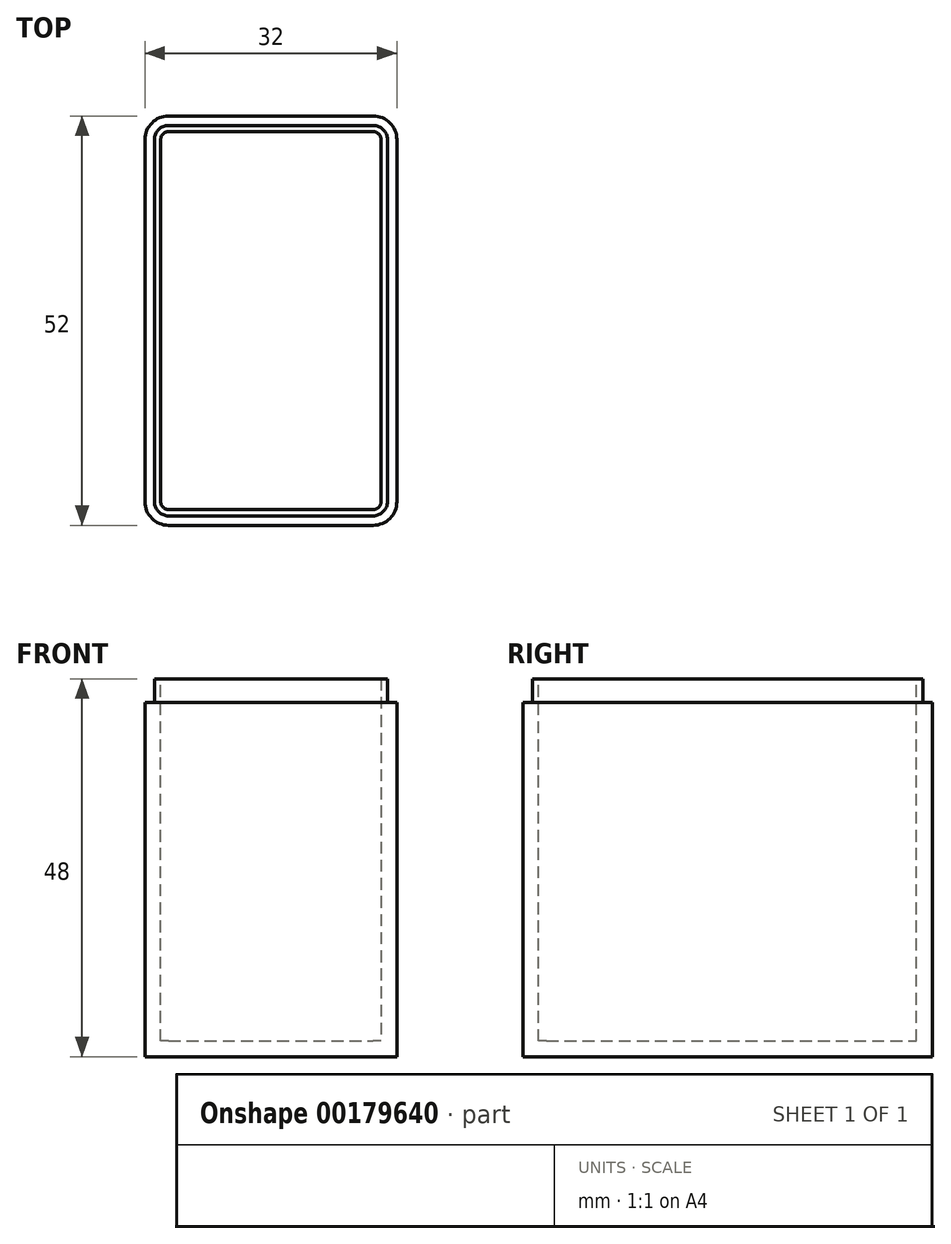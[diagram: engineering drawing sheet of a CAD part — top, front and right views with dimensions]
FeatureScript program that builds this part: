
annotation { "Feature Type Name" : "Feature", "Feature Type Description" : "" }
export const myFeature = defineFeature(function(context is Context, id is Id, definition is map)
    precondition{}
    {
        {
            var Q0;
            Q0=qCreatedBy(makeId("Top.planeOp"),FACE);
            var sketch = newSketch(context, id + "F0", { "sketchPlane" : qUnion([Q0])});
            skLineSegment(sketch, "E0.bottom", {"start": v(3, 0) * mm, "end": v(29, 0) * mm});
            skLineSegment(sketch, "E0.top", {"start": v(3, 52) * mm, "end": v(29, 52) * mm});
            skLineSegment(sketch, "E0.left", {"start": v(0, 3) * mm, "end": v(0, 49) * mm});
            skLineSegment(sketch, "E0.right", {"start": v(32, 3) * mm, "end": v(32, 49) * mm});
            skPoint(sketch, "E1.visualSharp", {"position": v(0, 52) * mm});
            skArc(sketch, "E1.filletArc", {"start": v(3, 52) * mm, "mid": v(0.88, 51.12) * mm, "end": v(0, 49) * mm});
            skPoint(sketch, "E2.visualSharp", {"position": v(32, 52) * mm});
            skArc(sketch, "E2.filletArc", {"start": v(32, 49) * mm, "mid": v(31.12, 51.12) * mm, "end": v(29, 52) * mm});
            skPoint(sketch, "E3.visualSharp", {"position": v(32, 0) * mm});
            skArc(sketch, "E3.filletArc", {"start": v(29, 0) * mm, "mid": v(31.12, 0.88) * mm, "end": v(32, 3) * mm});
            skPoint(sketch, "E4.visualSharp", {"position": v(0, 0) * mm});
            skArc(sketch, "E4.filletArc", {"start": v(0, 3) * mm, "mid": v(0.88, 0.88) * mm, "end": v(3, 0) * mm});
            skSolve(sketch);
        }
        {
            var Q0;
            Q0=makeQuery(id+"F0.imprint","IMPRINT",FACE,{"disambiguationData":[TD([[makeQuery(id+"F0.imprint","IMPRINT",EDGE,{"derivedFrom":sQuery(id+"F0.wireOp",EDGE,"E0.bottom")}),1.0]])]});
            extrude(context, id + "F1", {"entities" : qUnion([Q0]), "depth" : 45 * mm});
        }
        {
            var Q0;
            Q0=makeQuery(id+"F1.opExtrude","CAP_FACE",FACE,{"disambiguationData":[OSD([sQuery(id+"F0.wireOp",EDGE,"E0.bottom"),sQuery(id+"F0.wireOp",EDGE,"E0.top"),sQuery(id+"F0.wireOp",EDGE,"E0.left"),sQuery(id+"F0.wireOp",EDGE,"E0.right"),sQuery(id+"F0.wireOp",EDGE,"E1.filletArc"),sQuery(id+"F0.wireOp",EDGE,"E2.filletArc"),sQuery(id+"F0.wireOp",EDGE,"E3.filletArc"),sQuery(id+"F0.wireOp",EDGE,"E4.filletArc")])],"isStart":false});
            shell(context, id + "F2", {"entities" : qUnion([Q0]), "thickness" : 2 * mm});
        }
        {
            var Q0;
            Q0=makeQuery(id+"F1.opExtrude","CAP_FACE",FACE,{"disambiguationData":[OSD([sQuery(id+"F0.wireOp",EDGE,"E0.bottom"),sQuery(id+"F0.wireOp",EDGE,"E0.top"),sQuery(id+"F0.wireOp",EDGE,"E0.left"),sQuery(id+"F0.wireOp",EDGE,"E0.right"),sQuery(id+"F0.wireOp",EDGE,"E1.filletArc"),sQuery(id+"F0.wireOp",EDGE,"E2.filletArc"),sQuery(id+"F0.wireOp",EDGE,"E3.filletArc"),sQuery(id+"F0.wireOp",EDGE,"E4.filletArc")])],"isStart":false});
            var sketch = newSketch(context, id + "F3", { "sketchPlane" : qUnion([Q0])});
            skLineSegment(sketch, "E5.0", {"start": v(3, 2) * mm, "end": v(29, 2) * mm});
            skArc(sketch, "E6.0", {"start": v(2, 3) * mm, "mid": v(2.3, 2.3) * mm, "end": v(3, 2) * mm});
            skLineSegment(sketch, "E7.0", {"start": v(2, 3) * mm, "end": v(2, 49) * mm});
            skArc(sketch, "E8.0", {"start": v(3, 50) * mm, "mid": v(2.3, 49.7) * mm, "end": v(2, 49) * mm});
            skLineSegment(sketch, "E9.0", {"start": v(3, 50) * mm, "end": v(29, 50) * mm});
            skArc(sketch, "E10.0", {"start": v(30, 49) * mm, "mid": v(29.7, 49.7) * mm, "end": v(29, 50) * mm});
            skLineSegment(sketch, "E11.0", {"start": v(30, 3) * mm, "end": v(30, 49) * mm});
            skArc(sketch, "E12.0", {"start": v(29, 2) * mm, "mid": v(29.7, 2.3) * mm, "end": v(30, 3) * mm});
            skArc(sketch, "E13.0", {"start": v(29, 0) * mm, "mid": v(31.12, 0.88) * mm, "end": v(32, 3) * mm});
            skArc(sketch, "E14.0", {"start": v(0, 3) * mm, "mid": v(0.88, 0.88) * mm, "end": v(3, 0) * mm});
            skArc(sketch, "E15.0", {"start": v(3, 52) * mm, "mid": v(0.88, 51.12) * mm, "end": v(0, 49) * mm});
            skArc(sketch, "E16.0", {"start": v(32, 49) * mm, "mid": v(31.12, 51.12) * mm, "end": v(29, 52) * mm});
            skLineSegment(sketch, "E17.0", {"start": v(3, 52) * mm, "end": v(29, 52) * mm});
            skLineSegment(sketch, "E18.0", {"start": v(32, 3) * mm, "end": v(32, 49) * mm});
            skLineSegment(sketch, "E19.0", {"start": v(0, 3) * mm, "end": v(0, 49) * mm});
            skLineSegment(sketch, "E20.0", {"start": v(3, 0) * mm, "end": v(29, 0) * mm});
            skLineSegment(sketch, "E21.0", {"start": v(3, 50.8) * mm, "end": v(29, 50.8) * mm});
            skArc(sketch, "E21.1", {"start": v(30.8, 49) * mm, "mid": v(30.27, 50.27) * mm, "end": v(29, 50.8) * mm});
            skArc(sketch, "E21.2", {"start": v(3, 50.8) * mm, "mid": v(1.73, 50.27) * mm, "end": v(1.2, 49) * mm});
            skLineSegment(sketch, "E21.3", {"start": v(30.8, 3) * mm, "end": v(30.8, 49) * mm});
            skLineSegment(sketch, "E21.4", {"start": v(1.2, 3) * mm, "end": v(1.2, 49) * mm});
            skArc(sketch, "E21.5", {"start": v(1.2, 3) * mm, "mid": v(1.73, 1.73) * mm, "end": v(3, 1.2) * mm});
            skLineSegment(sketch, "E21.6", {"start": v(3, 1.2) * mm, "end": v(29, 1.2) * mm});
            skArc(sketch, "E21.7", {"start": v(29, 1.2) * mm, "mid": v(30.27, 1.73) * mm, "end": v(30.8, 3) * mm});
            skSolve(sketch);
        }
        {
            var Q0;
            Q0=makeQuery(id+"F3.imprint","IMPRINT",FACE,{"disambiguationData":[TD([[makeQuery(id+"F3.imprint","IMPRINT",EDGE,{"derivedFrom":sQuery(id+"F3.wireOp",EDGE,"E5.0")}),-1.0]])]});
            var Q1;
            Q1=sQuery(id+"F3.wireOp",EDGE,"E9.0");
            var Q2;
            Q2=sQuery(id+"F3.wireOp",EDGE,"E21.0");
            var Q3;
            Q3=sQuery(id+"F3.wireOp",EDGE,"E21.2");
            var Q4;
            Q4=sQuery(id+"F3.wireOp",EDGE,"E8.0");
            var Q5;
            Q5=sQuery(id+"F3.wireOp",EDGE,"E21.4");
            var Q6;
            Q6=sQuery(id+"F3.wireOp",EDGE,"E7.0");
            var Q7;
            Q7=sQuery(id+"F3.wireOp",EDGE,"E10.0");
            var Q8;
            Q8=sQuery(id+"F3.wireOp",EDGE,"E21.1");
            var Q9;
            Q9=sQuery(id+"F3.wireOp",EDGE,"E21.3");
            var Q10;
            Q10=sQuery(id+"F3.wireOp",EDGE,"E11.0");
            var Q11;
            Q11=sQuery(id+"F3.wireOp",EDGE,"E21.7");
            var Q12;
            Q12=sQuery(id+"F3.wireOp",EDGE,"E12.0");
            var Q13;
            Q13=sQuery(id+"F3.wireOp",EDGE,"E5.0");
            var Q14;
            Q14=sQuery(id+"F3.wireOp",EDGE,"E21.6");
            var Q15;
            Q15=sQuery(id+"F3.wireOp",EDGE,"E6.0");
            var Q16;
            Q16=sQuery(id+"F3.wireOp",EDGE,"E21.5");
            extrude(context, id + "F4", {"entities" : qUnion([Q0]), "operationType" : NewBodyOperationType.ADD, "surfaceEntities" : qUnion([Q1, Q2, Q3, Q4, Q5, Q6, Q7, Q8, Q9, Q10, Q11, Q12, Q13, Q14, Q15, Q16]), "depth" : 3 * mm});
        }
    });
